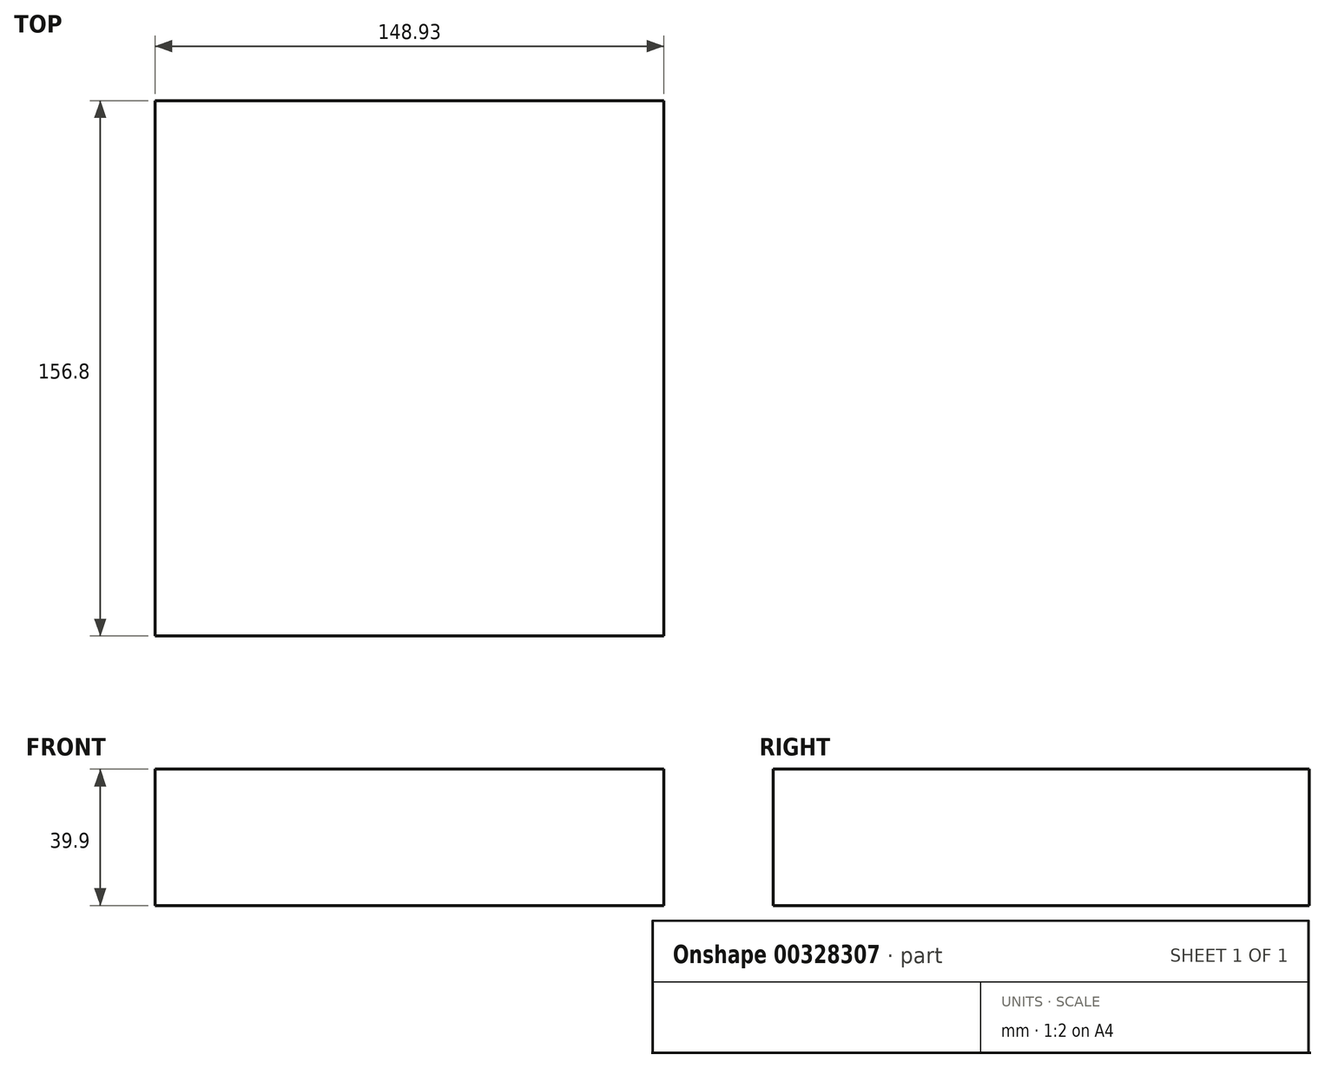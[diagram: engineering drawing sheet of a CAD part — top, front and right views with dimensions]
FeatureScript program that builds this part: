
annotation { "Feature Type Name" : "Feature", "Feature Type Description" : "" }
export const myFeature = defineFeature(function(context is Context, id is Id, definition is map)
    precondition{}
    {
        {
            var Q0;
            Q0=qCreatedBy(makeId("Top.planeOp"),FACE);
            var sketch = newSketch(context, id + "F0", { "sketchPlane" : qUnion([Q0])});
            skLineSegment(sketch, "E0.bottom", {"start": v(-75.01, -79.05) * mm, "end": v(73.92, -79.05) * mm});
            skLineSegment(sketch, "E0.top", {"start": v(-75.01, 77.75) * mm, "end": v(73.92, 77.75) * mm});
            skLineSegment(sketch, "E0.left", {"start": v(-75.01, -79.05) * mm, "end": v(-75.01, 77.75) * mm});
            skLineSegment(sketch, "E0.right", {"start": v(73.92, -79.05) * mm, "end": v(73.92, 77.75) * mm});
            skSolve(sketch);
        }
        {
            var Q0;
            Q0=makeQuery(id+"F0.imprint","IMPRINT",FACE,{"disambiguationData":[TD([[makeQuery(id+"F0.imprint","IMPRINT",EDGE,{"derivedFrom":sQuery(id+"F0.wireOp",EDGE,"E0.bottom")}),1.0]])]});
            extrude(context, id + "F1", {"entities" : qUnion([Q0]), "depth" : 39.9 * mm});
        }
    });
